# Revit family: 304_Green_2 AB-_
name_source: partatom
category: Pipe Accessories
units: mm (PartAtom-declared; Revit-internal decimal feet)

## family parameters
Always vertical = Yes
Cut with Voids When Loaded = No
Part Type = Valve - Breaks Into
Round Connector Dimension = Use Diameter
Shared = No
Work Plane-Based = No

## types (2) — shared parameters
CAT0 = Yes
Description = Green.2 - Pressure Independent Control Valve
L1 = 26 mm
L1__ve = -26 mm
L2 = 77 mm
L2D = 128 mm
L2D_Min = 3048 mm  [stored 10 ft]
L4 = 11 mm  [stored 0.0360892 ft]
LA = 75 mm  [stored 0.246063 ft]
LL = 64 mm  [stored 0.209974 ft]
Manufacturer = FlowCon
QmdConnectorList = 301;D;302;D
R3 = 6 mm  [stored 0.019685 ft]
RA = 30 mm  [stored 0.0984252 ft]
URL = http://flowcon.com
magiPartTypeId = 304
magiProductFamilyId = Green.2 AB-*
zero-valued in all types: MC_Default_elevation

## per-type parameters (varying)
| type | CenSd_RN_6 | CenSd_SW_6 | D | H11 | H12 | L3 | L3__ve | L5 | L6 | L6__ve | L7 | R1 | R2 | RN | SW | W2D | magiProductId |
| G.2.22.14.B | 11 mm  [stored 0.0360892 ft] | 16 mm | 25 mm | 39 mm | 88 mm | 102 mm | -102 mm | 51 mm | 50 mm  [stored 0.164042 ft] | -50 mm  [stored -0.164042 ft] | 41 mm  [stored 0.134514 ft] | 14 mm  [stored 0.0459318 ft] | 16 mm | 13 mm  [stored 0.0426509 ft] | 18 mm  [stored 0.0590551 ft] | 25 mm  [stored 0.082021 ft] | Green.2 AB-25 |
| G.2.22.15.B | 14 mm  [stored 0.0459318 ft] | 20 mm  [stored 0.0656168 ft] | 32 mm | 37 mm | 86 mm | 99 mm | -99 mm | 50 mm  [stored 0.164042 ft] | 65 mm  [stored 0.213255 ft] | -65 mm  [stored -0.213255 ft] | 56 mm  [stored 0.183727 ft] | 17 mm | 21 mm | 17 mm | 23 mm | 32 mm  [stored 0.104987 ft] | Green.2 AB-32 |

note: column(s) folded — value = type name in every type: magiProductCode

note: [stored X ft] marks values corroborated as IEEE doubles in the binary element streams (Revit-internal decimal feet)

## geometry (parser evidence)
native form markers: Sweep x2
no freeform markers — native parametric forms only
